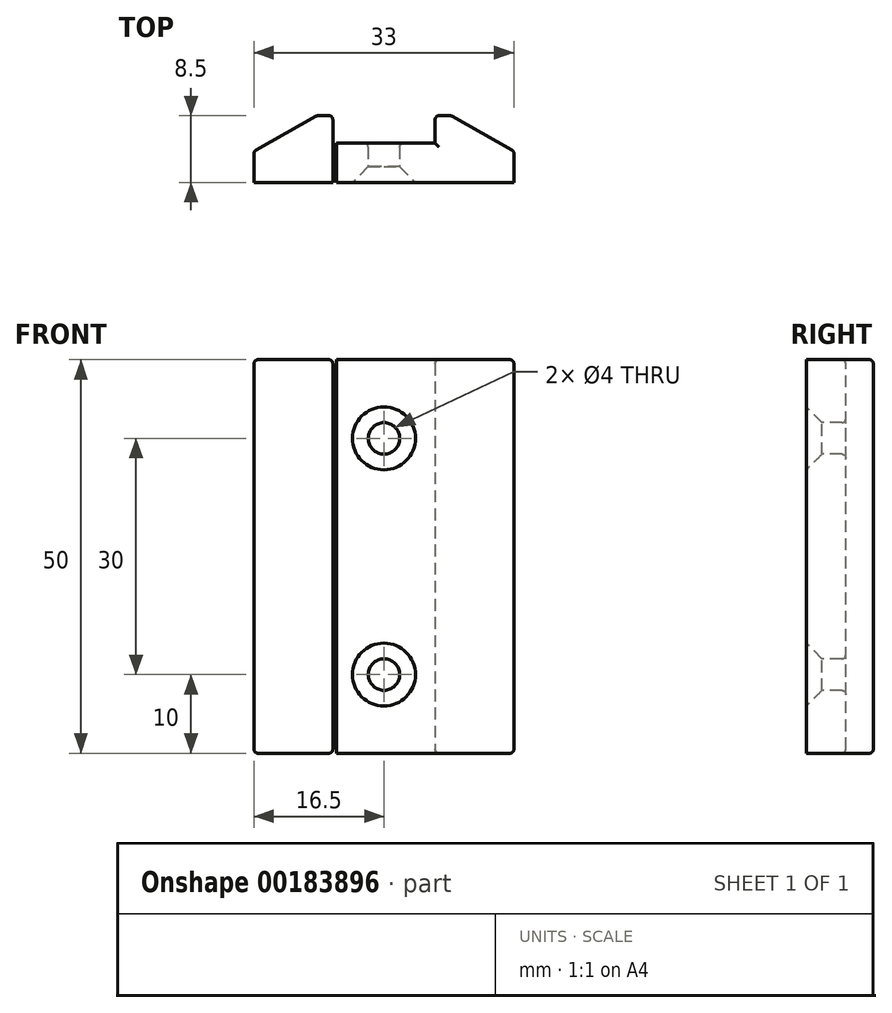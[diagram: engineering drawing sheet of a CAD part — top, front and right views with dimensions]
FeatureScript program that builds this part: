
annotation { "Feature Type Name" : "Feature", "Feature Type Description" : "" }
export const myFeature = defineFeature(function(context is Context, id is Id, definition is map)
    precondition{}
    {
        {
            var Q0;
            Q0=qCreatedBy(makeId("Front.planeOp"),FACE);
            var sketch = newSketch(context, id + "F0", { "sketchPlane" : qUnion([Q0])});
            skLineSegment(sketch, "E0.bottom", {"start": v(6, -25) * mm, "end": v(-6, -25) * mm});
            skLineSegment(sketch, "E0.top", {"start": v(6, 25) * mm, "end": v(-6, 25) * mm});
            skLineSegment(sketch, "E0.left", {"start": v(6, -25) * mm, "end": v(6, 25) * mm});
            skLineSegment(sketch, "E0.right", {"start": v(-6, -25) * mm, "end": v(-6, 25) * mm});
            skPoint(sketch, "E0.middle", {"position": v(0, 0) * mm});
            skLineSegment(sketch, "E1.bottom", {"start": v(-6, 25) * mm, "end": v(-16.5, 25) * mm});
            skLineSegment(sketch, "E1.top", {"start": v(-6, -25) * mm, "end": v(-16.5, -25) * mm});
            skLineSegment(sketch, "E1.left", {"start": v(-6, 25) * mm, "end": v(-6, -25) * mm});
            skLineSegment(sketch, "E1.right", {"start": v(-16.5, 25) * mm, "end": v(-16.5, -25) * mm});
            skLineSegment(sketch, "E2.MirrorCS", {"start": v(6.5, 25) * mm, "end": v(16.5, 25) * mm});
            skLineSegment(sketch, "E3.MirrorCS", {"start": v(16.5, 25) * mm, "end": v(16.5, -25) * mm});
            skLineSegment(sketch, "E4.MirrorCS", {"start": v(6.5, -25) * mm, "end": v(16.5, -25) * mm});
            skLineSegment(sketch, "E5.0", {"start": v(-6.5, 25) * mm, "end": v(-6.5, -25) * mm});
            skLineSegment(sketch, "E6.MirrorCS", {"start": v(6.5, 25) * mm, "end": v(6.5, -25) * mm});
            skLineSegment(sketch, "E7", {"start": v(0, 25) * mm, "end": v(0, -25) * mm, "construction": true});
            skLineSegment(sketch, "E8", {"start": v(-16.5, -15) * mm, "end": v(16.5, -15) * mm, "construction": true});
            skLineSegment(sketch, "E9", {"start": v(-16.5, 15) * mm, "end": v(16.5, 15) * mm, "construction": true});
            skCircle(sketch, "E10", {"center": v(0, 15) * mm, "radius": 2 * mm});
            skCircle(sketch, "E11", {"center": v(0, -15) * mm, "radius": 2 * mm});
            skLineSegment(sketch, "E12", {"start": v(6.5, 25) * mm, "end": v(6, 25) * mm});
            skLineSegment(sketch, "E13", {"start": v(6.5, -25) * mm, "end": v(6, -25) * mm});
            skSolve(sketch);
        }
        {
            var Q0;
            Q0=makeQuery(id+"F0.imprint","IMPRINT",FACE,{"disambiguationData":[TD([[makeQuery(id+"F0.imprint","IMPRINT",EDGE,{"derivedFrom":sQuery(id+"F0.wireOp",EDGE,"E0.bottom")}),-1.0]])]});
            var Q1;
            {var subQ1=sQuery(id+"F0.wireOp",EDGE,"E1.right");Q1=makeQuery(id+"F0.imprint","IMPRINT",FACE,{"disambiguationData":[TD([[makeQuery(id+"F0.imprint","IMPRINT",EDGE,{"derivedFrom":subQ1}),1.0]])]});}
            var Q2;
            {var subQ0=sQuery(id+"F0.wireOp",EDGE,"E1.left");Q2=makeQuery(id+"F0.imprint","IMPRINT",FACE,{"disambiguationData":[TD([[makeQuery(id+"F0.imprint","IMPRINT",EDGE,{"derivedFrom":subQ0}),-1.0]])]});}
            var Q3;
            Q3=makeQuery(id+"F0.imprint","IMPRINT",FACE,{"disambiguationData":[TD([[makeQuery(id+"F0.imprint","IMPRINT",EDGE,{"derivedFrom":sQuery(id+"F0.wireOp",EDGE,"E0.left")}),-1.0]])]});
            var Q4;
            Q4=makeQuery(id+"F0.imprint","IMPRINT",FACE,{"disambiguationData":[TD([[makeQuery(id+"F0.imprint","IMPRINT",EDGE,{"derivedFrom":sQuery(id+"F0.wireOp",EDGE,"E2.MirrorCS")}),-1.0]])]});
            extrude(context, id + "F1", {"entities" : qUnion([Q0, Q1, Q2, Q3, Q4]), "oppositeDirection" : true, "depth" : 5 * mm});
        }
        {
            var Q0;
            {var subQ0=sQuery(id+"F0.wireOp",EDGE,"E1.right");Q0=makeQuery(id+"F0.imprint","IMPRINT",FACE,{"disambiguationData":[TD([[makeQuery(id+"F0.imprint","IMPRINT",EDGE,{"derivedFrom":subQ0}),1.0]])]});}
            var Q1;
            {var subQ0=sQuery(id+"F0.wireOp",EDGE,"E3.MirrorCS");Q1=makeQuery(id+"F0.imprint","IMPRINT",FACE,{"disambiguationData":[TD([[makeQuery(id+"F0.imprint","IMPRINT",EDGE,{"derivedFrom":subQ0}),-1.0]])]});}
            extrude(context, id + "F2", {"entities" : qUnion([Q0, Q1]), "operationType" : NewBodyOperationType.ADD, "oppositeDirection" : true, "depth" : 8.5 * mm});
        }
        {
            var Q0;
            Q0=makeQuery(id+"F2.opExtrude","CAP_EDGE",EDGE,{"disambiguationData":[OSD([sQuery(id+"F0.wireOp",EDGE,"E1.right")])],"isStart":false});
            chamfer(context, id + "F3", {"entities" : qUnion([Q0]), "chamferType" : ChamferType.TWO_OFFSETS, "width1" : 4.5 * mm, "oppositeDirection" : false, "width2" : 8 * mm});
        }
        {
            var Q0;
            Q0=makeQuery(id+"F2.opExtrude","CAP_EDGE",EDGE,{"disambiguationData":[OSD([sQuery(id+"F0.wireOp",EDGE,"E3.MirrorCS")])],"isStart":false});
            chamfer(context, id + "F4", {"entities" : qUnion([Q0]), "chamferType" : ChamferType.TWO_OFFSETS, "width1" : 4.5 * mm, "oppositeDirection" : true, "width2" : 8 * mm, "tangentPropagation" : true});
        }
        {
            var Q0;
            Q0=sQuery(id+"F0.wireOp",VERTEX,"E10.center");
            var Q1;
            Q1=sQuery(id+"F0.wireOp",VERTEX,"E11.center");
            var Q2;
            Q2=makeQuery(id+"F1.opExtrude","SWEPT_BODY",BODY,{"disambiguationData":[OSD([sQuery(id+"F0.wireOp",EDGE,"E0.bottom"),sQuery(id+"F0.wireOp",EDGE,"E0.top"),sQuery(id+"F0.wireOp",EDGE,"E1.bottom"),sQuery(id+"F0.wireOp",EDGE,"E1.top"),sQuery(id+"F0.wireOp",EDGE,"E1.right"),sQuery(id+"F0.wireOp",EDGE,"E2.MirrorCS"),sQuery(id+"F0.wireOp",EDGE,"E3.MirrorCS"),sQuery(id+"F0.wireOp",EDGE,"E4.MirrorCS")])]});
            hole(context, id + "F5", {"style" : HoleStyle.C_SINK, "endStyle" : HoleEndStyle.THROUGH, "holeDiameter" : 4 * mm, "cSinkDiameter" : 8 * mm, "cSinkAngle" : 90 * degree, "locations" : qUnion([Q0, Q1]), "scope" : qUnion([Q2]), "isTappedThrough" : true});
        }
        {
            var Q0;
            Q0=makeQuery(id+"Fde6kDLOxshh8E3_1.opExtrude","SWEPT_FACE",FACE,{"disambiguationData":[OSD([sQuery(id+"F0.wireOp",EDGE,"T33Nxz9f-G0tn-xnhC-FvTE-fY2xuErrY73N")])]});
            var Q1;
            Q1=makeQuery(id+"Fde6kDLOxshh8E3_1.opExtrude","SWEPT_FACE",FACE,{"disambiguationData":[OSD([sQuery(id+"F0.wireOp",EDGE,"da0ba401-8d94-4197-b795-813e0965d0f9")])]});
            var Q2;
            Q2=makeQuery(id+"Fde6kDLOxshh8E3_1.opExtrude","SWEPT_FACE",FACE,{"disambiguationData":[OSD([sQuery(id+"F0.wireOp",EDGE,"e77e1b9a-007d-4c83-9508-98feed9c690b")])]});
            var Q3;
            Q3=makeQuery(id+"Fde6kDLOxshh8E3_1.opExtrude","SWEPT_FACE",FACE,{"disambiguationData":[OSD([sQuery(id+"F0.wireOp",EDGE,"39f81b70-e8c2-4875-9376-20bc0b2a6c3b")])]});
            var Q4;
            Q4=makeQuery(id+"F4.opChamfer","BLEND_FACE",FACE,{"disambiguationData":[OSD([sQuery(id+"F0.wireOp",EDGE,"E3.MirrorCS")])]});
            var Q5;
            Q5=makeQuery(id+"F2.opExtrude","CAP_FACE",FACE,{"disambiguationData":[OSD([sQuery(id+"F0.wireOp",EDGE,"E2.MirrorCS"),sQuery(id+"F0.wireOp",EDGE,"E3.MirrorCS"),sQuery(id+"F0.wireOp",EDGE,"E4.MirrorCS"),sQuery(id+"F0.wireOp",EDGE,"E6.MirrorCS"),sQuery(id+"F0.wireOp",EDGE,"539f9750-dc91-464b-a573-112b15fa390c.0"),sQuery(id+"F0.wireOp",EDGE,"539f9750-dc91-464b-a573-112b15fa390c.1"),sQuery(id+"F0.wireOp",EDGE,"539f9750-dc91-464b-a573-112b15fa390c.2"),sQuery(id+"F0.wireOp",EDGE,"539f9750-dc91-464b-a573-112b15fa390c.3"),sQuery(id+"F0.wireOp",EDGE,"539f9750-dc91-464b-a573-112b15fa390c.4"),sQuery(id+"F0.wireOp",EDGE,"539f9750-dc91-464b-a573-112b15fa390c.5"),sQuery(id+"F0.wireOp",EDGE,"a8e38511-2c6b-4656-bbe2-a021e63cbe50.0"),sQuery(id+"F0.wireOp",EDGE,"a8e38511-2c6b-4656-bbe2-a021e63cbe50.1"),sQuery(id+"F0.wireOp",EDGE,"a8e38511-2c6b-4656-bbe2-a021e63cbe50.2"),sQuery(id+"F0.wireOp",EDGE,"a8e38511-2c6b-4656-bbe2-a021e63cbe50.3"),sQuery(id+"F0.wireOp",EDGE,"a8e38511-2c6b-4656-bbe2-a021e63cbe50.4"),sQuery(id+"F0.wireOp",EDGE,"a8e38511-2c6b-4656-bbe2-a021e63cbe50.5")])],"isStart":false});
            var Q6;
            Q6=makeQuery(id+"F2.opExtrude","CAP_FACE",FACE,{"disambiguationData":[OSD([sQuery(id+"F0.wireOp",EDGE,"E1.bottom"),sQuery(id+"F0.wireOp",EDGE,"E1.top"),sQuery(id+"F0.wireOp",EDGE,"E1.right"),sQuery(id+"F0.wireOp",EDGE,"E5.0"),sQuery(id+"F0.wireOp",EDGE,"23c44e91-364b-44a9-8542-abd9dcfbb523.0"),sQuery(id+"F0.wireOp",EDGE,"23c44e91-364b-44a9-8542-abd9dcfbb523.1"),sQuery(id+"F0.wireOp",EDGE,"23c44e91-364b-44a9-8542-abd9dcfbb523.2"),sQuery(id+"F0.wireOp",EDGE,"23c44e91-364b-44a9-8542-abd9dcfbb523.3"),sQuery(id+"F0.wireOp",EDGE,"23c44e91-364b-44a9-8542-abd9dcfbb523.4"),sQuery(id+"F0.wireOp",EDGE,"23c44e91-364b-44a9-8542-abd9dcfbb523.5"),sQuery(id+"F0.wireOp",EDGE,"c08f9198-67c1-4cca-93f6-4b56ce47e8c6.0"),sQuery(id+"F0.wireOp",EDGE,"c08f9198-67c1-4cca-93f6-4b56ce47e8c6.1"),sQuery(id+"F0.wireOp",EDGE,"c08f9198-67c1-4cca-93f6-4b56ce47e8c6.2"),sQuery(id+"F0.wireOp",EDGE,"c08f9198-67c1-4cca-93f6-4b56ce47e8c6.3"),sQuery(id+"F0.wireOp",EDGE,"c08f9198-67c1-4cca-93f6-4b56ce47e8c6.4"),sQuery(id+"F0.wireOp",EDGE,"c08f9198-67c1-4cca-93f6-4b56ce47e8c6.5")])],"isStart":false});
            var Q7;
            Q7=makeQuery(id+"F3.opChamfer","BLEND_FACE",FACE,{"disambiguationData":[OSD([sQuery(id+"F0.wireOp",EDGE,"E1.right")])]});
            var Q8;
            Q8=makeQuery(id+"F1.opExtrude","CAP_EDGE",EDGE,{"disambiguationData":[OSD([sQuery(id+"F0.wireOp",EDGE,"E11")])],"isStart":false});
            var Q9;
            Q9=makeQuery(id+"F1.opExtrude","CAP_EDGE",EDGE,{"disambiguationData":[OSD([sQuery(id+"F0.wireOp",EDGE,"E10")])],"isStart":false});
            var Q10;
            Q10=makeQuery(id+"F1.opExtrude","CAP_EDGE",EDGE,{"disambiguationData":[OSD([sQuery(id+"F0.wireOp",EDGE,"E0.bottom"),sQuery(id+"F0.wireOp",EDGE,"E1.top"),sQuery(id+"F0.wireOp",EDGE,"E4.MirrorCS"),sQuery(id+"F0.wireOp",EDGE,"E13")])],"isStart":false});
            var Q11;
            Q11=makeQuery(id+"F2.opExtrude","SWEPT_EDGE",EDGE,{"disambiguationData":[OSD([sQuery(id+"F0.wireOp",EDGE,"E4.MirrorCS"),sQuery(id+"F0.wireOp",EDGE,"E6.MirrorCS"),sQuery(id+"F0.wireOp",EDGE,"E13")])]});
            var Q12;
            Q12=makeQuery(id+"F2.opExtrude","SWEPT_EDGE",EDGE,{"disambiguationData":[OSD([sQuery(id+"F0.wireOp",EDGE,"E1.top"),sQuery(id+"F0.wireOp",EDGE,"E5.0")])]});
            var Q13;
            {var subQ0=sQuery(id+"F0.wireOp",EDGE,"E1.right");var subQ1=sQuery(id+"F0.wireOp",EDGE,"E1.top");Q13=makeQuery(id+"F2.boolean.opBoolean","MERGE",EDGE,{"derivedFrom":[makeQuery(id+"F1.opExtrude","SWEPT_EDGE",EDGE,{"disambiguationData":[OSD([subQ1,subQ0])]}),makeQuery(id+"F2.opExtrude","SWEPT_EDGE",EDGE,{"disambiguationData":[OSD([subQ1,subQ0])]})]});}
            var Q14;
            {var subQ0=sQuery(id+"F0.wireOp",EDGE,"E4.MirrorCS");var subQ1=sQuery(id+"F0.wireOp",EDGE,"E3.MirrorCS");Q14=makeQuery(id+"F2.boolean.opBoolean","MERGE",EDGE,{"derivedFrom":[makeQuery(id+"F1.opExtrude","SWEPT_EDGE",EDGE,{"disambiguationData":[OSD([subQ1,subQ0])]}),makeQuery(id+"F2.opExtrude","SWEPT_EDGE",EDGE,{"disambiguationData":[OSD([subQ1,subQ0])]})]});}
            var Q15;
            {var subQ0=sQuery(id+"F0.wireOp",EDGE,"E3.MirrorCS");var subQ1=sQuery(id+"F0.wireOp",EDGE,"E2.MirrorCS");Q15=makeQuery(id+"F2.boolean.opBoolean","MERGE",EDGE,{"derivedFrom":[makeQuery(id+"F1.opExtrude","SWEPT_EDGE",EDGE,{"disambiguationData":[OSD([subQ1,subQ0])]}),makeQuery(id+"F2.opExtrude","SWEPT_EDGE",EDGE,{"disambiguationData":[OSD([subQ1,subQ0])]})]});}
            var Q16;
            Q16=makeQuery(id+"F2.opExtrude","SWEPT_EDGE",EDGE,{"disambiguationData":[OSD([sQuery(id+"F0.wireOp",EDGE,"E2.MirrorCS"),sQuery(id+"F0.wireOp",EDGE,"E6.MirrorCS"),sQuery(id+"F0.wireOp",EDGE,"E12")])]});
            var Q17;
            Q17=makeQuery(id+"F1.opExtrude","CAP_EDGE",EDGE,{"disambiguationData":[OSD([sQuery(id+"F0.wireOp",EDGE,"E0.top"),sQuery(id+"F0.wireOp",EDGE,"E1.bottom"),sQuery(id+"F0.wireOp",EDGE,"E2.MirrorCS"),sQuery(id+"F0.wireOp",EDGE,"E12")])],"isStart":false});
            var Q18;
            Q18=makeQuery(id+"F2.opExtrude","SWEPT_EDGE",EDGE,{"disambiguationData":[OSD([sQuery(id+"F0.wireOp",EDGE,"E1.bottom"),sQuery(id+"F0.wireOp",EDGE,"E5.0")])]});
            var Q19;
            {var subQ0=sQuery(id+"F0.wireOp",EDGE,"E1.right");var subQ1=sQuery(id+"F0.wireOp",EDGE,"E1.bottom");Q19=makeQuery(id+"F2.boolean.opBoolean","MERGE",EDGE,{"derivedFrom":[makeQuery(id+"F1.opExtrude","SWEPT_EDGE",EDGE,{"disambiguationData":[OSD([subQ1,subQ0])]}),makeQuery(id+"F2.opExtrude","SWEPT_EDGE",EDGE,{"disambiguationData":[OSD([subQ1,subQ0])]})]});}
            fillet(context, id + "F6", {"entities" : qUnion([Q0, Q1, Q2, Q3, Q4, Q5, Q6, Q7, Q8, Q9, Q10, Q11, Q12, Q13, Q14, Q15, Q16, Q17, Q18, Q19]), "radius" : 0.5 * mm, "tangentPropagation" : true, "allowEdgeOverflow" : false});
        }
    });
